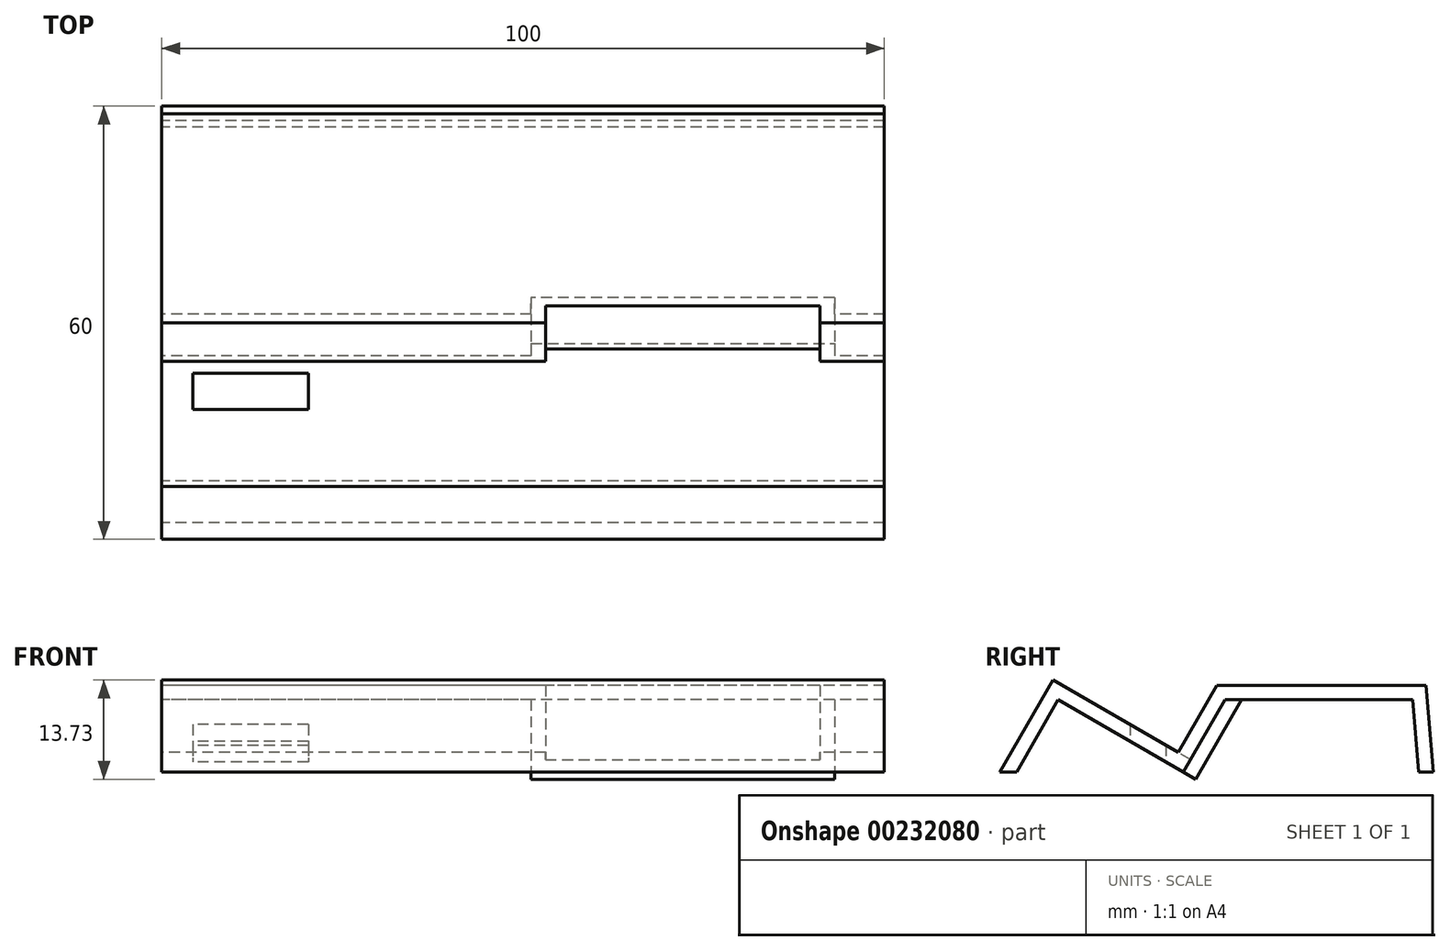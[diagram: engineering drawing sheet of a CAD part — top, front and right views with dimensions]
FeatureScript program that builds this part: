
annotation { "Feature Type Name" : "Feature", "Feature Type Description" : "" }
export const myFeature = defineFeature(function(context is Context, id is Id, definition is map)
    precondition{}
    {
        {
            var Q0;
            Q0=qCreatedBy(makeId("Right.planeOp"),FACE);
            var sketch = newSketch(context, id + "F0", { "sketchPlane" : qUnion([Q0])});
            skLineSegment(sketch, "E0", {"start": v(-30, 0) * mm, "end": v(-22.65, 12.73) * mm});
            skLineSegment(sketch, "E1", {"start": v(-22.65, 12.73) * mm, "end": v(-5.33, 2.73) * mm});
            skLineSegment(sketch, "E2", {"start": v(-5.33, 2.73) * mm, "end": v(0.02, 12) * mm});
            skLineSegment(sketch, "E3", {"start": v(0.02, 12) * mm, "end": v(28.95, 12) * mm});
            skLineSegment(sketch, "E4", {"start": v(28.95, 12) * mm, "end": v(30, 0) * mm});
            skLineSegment(sketch, "E5.0", {"start": v(27.12, 10) * mm, "end": v(28, 0) * mm, "construction": true});
            skLineSegment(sketch, "E5.1", {"start": v(-27.7, 0) * mm, "end": v(-21.92, 10) * mm, "construction": true});
            skLineSegment(sketch, "E5.2", {"start": v(-21.92, 10) * mm, "end": v(-4.6, 0) * mm, "construction": true});
            skLineSegment(sketch, "E5.3", {"start": v(-4.6, 0) * mm, "end": v(1.18, 10) * mm, "construction": true});
            skLineSegment(sketch, "E5.4", {"start": v(1.18, 10) * mm, "end": v(27.12, 10) * mm, "construction": true});
            skLineSegment(sketch, "E6", {"start": v(-30, 0) * mm, "end": v(-27.7, 0) * mm, "construction": true});
            skLineSegment(sketch, "E7.trimOffspring", {"start": v(28, 0) * mm, "end": v(30, 0) * mm, "construction": true});
            skLineSegment(sketch, "E8", {"start": v(-30, 0) * mm, "end": v(30, 0) * mm});
            skSolve(sketch);
        }
        {
            var Q0;
            Q0 = qSketchRegion(id + "F0", true);
            extrude(context, id + "F1", {"entities" : qUnion([Q0]), "endBound" : BoundingType.SYMMETRIC, "depth" : 100 * mm});
        }
        {
            var Q0;
            Q0=makeQuery(id+"F1.opExtrude","SWEPT_FACE",FACE,{"disambiguationData":[OSD([sQuery(id+"F0.wireOp",EDGE,"E1")])]});
            var sketch = newSketch(context, id + "F2", { "sketchPlane" : qUnion([Q0])});
            skLineSegment(sketch, "E9.bottom", {"start": v(3.1, -3.98) * mm, "end": v(41.1, -3.98) * mm});
            skLineSegment(sketch, "E9.top", {"start": v(3.1, -5.98) * mm, "end": v(41.1, -5.98) * mm});
            skLineSegment(sketch, "E9.left", {"start": v(3.1, -3.98) * mm, "end": v(3.1, -5.98) * mm});
            skLineSegment(sketch, "E9.right", {"start": v(41.1, -3.98) * mm, "end": v(41.1, -5.98) * mm});
            skSolve(sketch);
        }
        {
            var Q0;
            Q0 = qSketchRegion(id + "F2", true);
            extrude(context, id + "F3", {"entities" : qUnion([Q0]), "operationType" : NewBodyOperationType.REMOVE, "endBound" : BoundingType.THROUGH_ALL, "depth" : 25 * mm});
        }
        {
            var Q0;
            Q0=makeQuery(id+"F1.opExtrude","SWEPT_FACE",FACE,{"disambiguationData":[OSD([sQuery(id+"F0.wireOp",EDGE,"E8")])]});
            var Q1;
            Q1=makeQuery(id+"F1.opExtrude","CAP_FACE",FACE,{"disambiguationData":[OSD([sQuery(id+"F0.wireOp",EDGE,"E0"),sQuery(id+"F0.wireOp",EDGE,"E1"),sQuery(id+"F0.wireOp",EDGE,"E2"),sQuery(id+"F0.wireOp",EDGE,"E3"),sQuery(id+"F0.wireOp",EDGE,"E4"),sQuery(id+"F0.wireOp",EDGE,"E8")])],"isStart":false});
            var Q2;
            Q2=makeQuery(id+"F1.opExtrude","CAP_FACE",FACE,{"disambiguationData":[OSD([sQuery(id+"F0.wireOp",EDGE,"E0"),sQuery(id+"F0.wireOp",EDGE,"E1"),sQuery(id+"F0.wireOp",EDGE,"E2"),sQuery(id+"F0.wireOp",EDGE,"E3"),sQuery(id+"F0.wireOp",EDGE,"E4"),sQuery(id+"F0.wireOp",EDGE,"E8")])],"isStart":true});
            shell(context, id + "F4", {"entities" : qUnion([Q0, Q1, Q2]), "thickness" : 2 * mm});
        }
        {
            var Q0;
            Q0=qCreatedBy(makeId("Top.planeOp"),FACE);
            var sketch = newSketch(context, id + "F5", { "sketchPlane" : qUnion([Q0])});
            skLineSegment(sketch, "E10.bottom", {"start": v(-45.73, -7) * mm, "end": v(-29.73, -7) * mm});
            skLineSegment(sketch, "E10.top", {"start": v(-45.73, -12) * mm, "end": v(-29.73, -12) * mm});
            skLineSegment(sketch, "E10.left", {"start": v(-45.73, -7) * mm, "end": v(-45.73, -12) * mm});
            skLineSegment(sketch, "E10.right", {"start": v(-29.73, -7) * mm, "end": v(-29.73, -12) * mm});
            skSolve(sketch);
        }
        {
            var Q0;
            Q0 = qSketchRegion(id + "F5", true);
            extrude(context, id + "F6", {"entities" : qUnion([Q0]), "operationType" : NewBodyOperationType.REMOVE, "endBound" : BoundingType.THROUGH_ALL, "depth" : 25 * mm});
        }
    });
